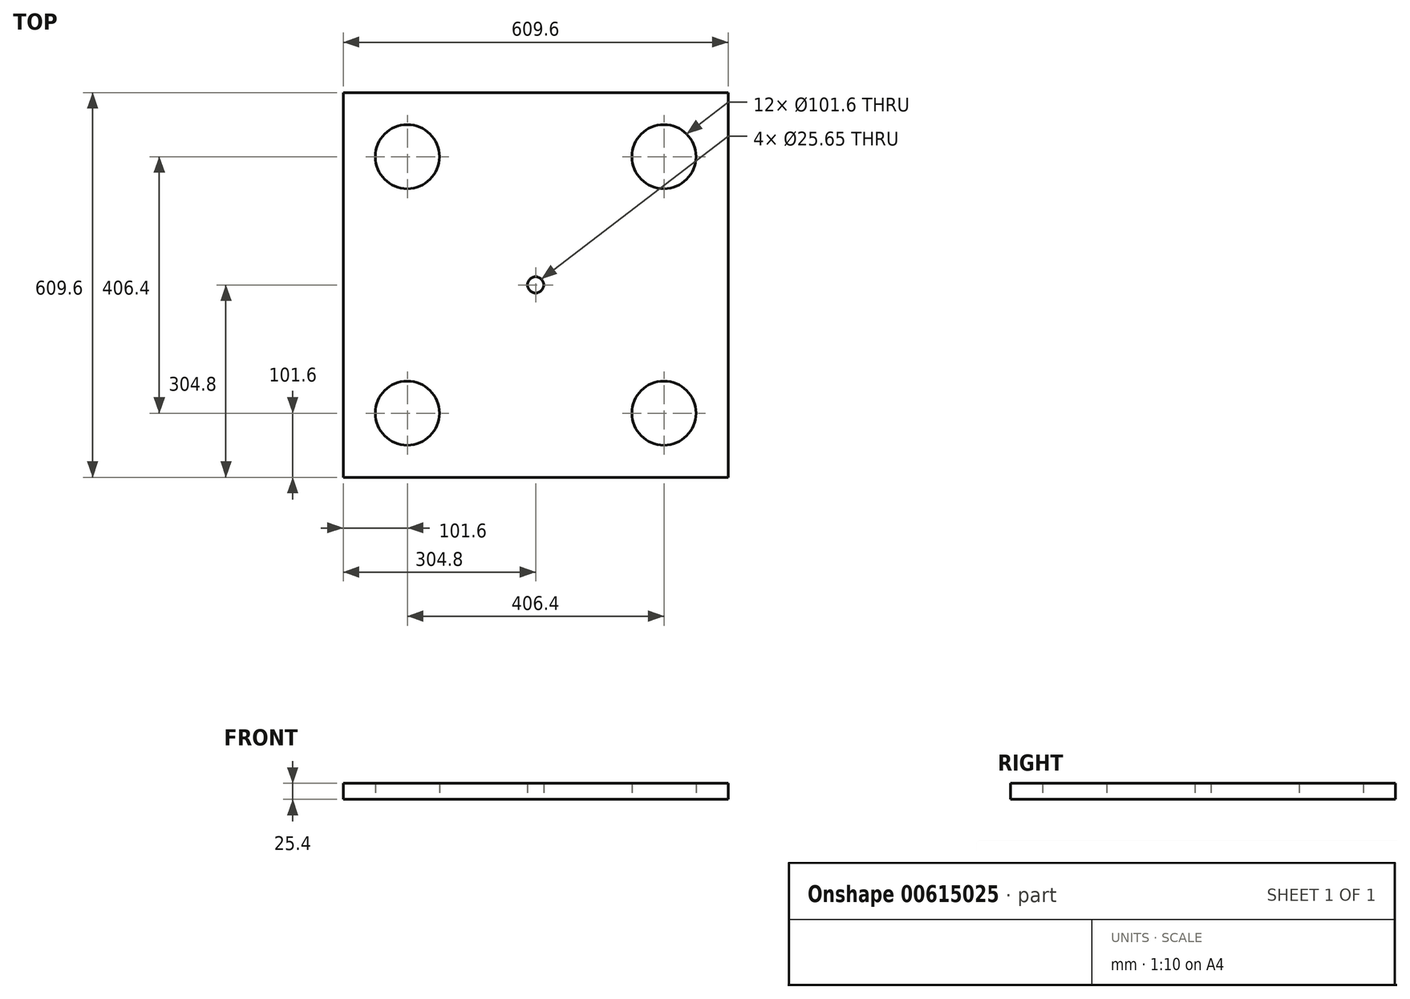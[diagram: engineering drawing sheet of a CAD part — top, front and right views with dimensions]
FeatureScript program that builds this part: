
annotation { "Feature Type Name" : "Feature", "Feature Type Description" : "" }
export const myFeature = defineFeature(function(context is Context, id is Id, definition is map)
    precondition{}
    {
        {
            var Q0;
            Q0=qCreatedBy(makeId("Top.planeOp"),FACE);
            var sketch = newSketch(context, id + "F0", { "sketchPlane" : qUnion([Q0])});
            skLineSegment(sketch, "E0.bottom", {"start": v(304.8, 304.8) * mm, "end": v(-304.8, 304.8) * mm});
            skLineSegment(sketch, "E0.top", {"start": v(304.8, -304.8) * mm, "end": v(-304.8, -304.8) * mm});
            skLineSegment(sketch, "E0.left", {"start": v(304.8, 304.8) * mm, "end": v(304.8, -304.8) * mm});
            skLineSegment(sketch, "E0.right", {"start": v(-304.8, 304.8) * mm, "end": v(-304.8, -304.8) * mm});
            skPoint(sketch, "E0.middle", {"position": v(0, 0) * mm});
            skLineSegment(sketch, "E1.0", {"start": v(203.2, 203.2) * mm, "end": v(-203.2, 203.2) * mm, "construction": true});
            skLineSegment(sketch, "E1.1", {"start": v(203.2, 203.2) * mm, "end": v(203.2, -203.2) * mm, "construction": true});
            skLineSegment(sketch, "E1.2", {"start": v(203.2, -203.2) * mm, "end": v(-203.2, -203.2) * mm, "construction": true});
            skLineSegment(sketch, "E1.3", {"start": v(-203.2, 203.2) * mm, "end": v(-203.2, -203.2) * mm, "construction": true});
            skCircle(sketch, "E2", {"center": v(-203.2, 203.2) * mm, "radius": 50.8 * mm});
            skCircle(sketch, "E3.MirrorC", {"center": v(203.2, 203.2) * mm, "radius": 50.8 * mm});
            skCircle(sketch, "E4.MirrorC", {"center": v(203.2, -203.2) * mm, "radius": 50.8 * mm});
            skCircle(sketch, "E5.MirrorC", {"center": v(-203.2, -203.2) * mm, "radius": 50.8 * mm});
            skCircle(sketch, "E6", {"center": v(0, 0) * mm, "radius": 12.83 * mm});
            skSolve(sketch);
        }
        {
            var Q0;
            Q0=makeQuery(id+"F0.imprint","IMPRINT",FACE,{"disambiguationData":[TD([[makeQuery(id+"F0.imprint","IMPRINT",EDGE,{"derivedFrom":sQuery(id+"F0.wireOp",EDGE,"E0.bottom")}),1.0]])]});
            extrude(context, id + "F1", {"entities" : qUnion([Q0]), "depth" : 25.4 * mm, "offsetDistance" : 25.4 * mm});
        }
        {
            var Q0;
            Q0=makeQuery(id+"F0.imprint","IMPRINT",FACE,{"disambiguationData":[TD([[makeQuery(id+"F0.imprint","IMPRINT",EDGE,{"derivedFrom":sQuery(id+"F0.wireOp",EDGE,"E5.MirrorC")}),-1.0]])]});
            var Q1;
            Q1=makeQuery(id+"F0.imprint","IMPRINT",FACE,{"disambiguationData":[TD([[makeQuery(id+"F0.imprint","IMPRINT",EDGE,{"derivedFrom":sQuery(id+"F0.wireOp",EDGE,"E4.MirrorC")}),1.0]])]});
            var Q2;
            Q2=makeQuery(id+"F0.imprint","IMPRINT",FACE,{"disambiguationData":[TD([[makeQuery(id+"F0.imprint","IMPRINT",EDGE,{"derivedFrom":sQuery(id+"F0.wireOp",EDGE,"E3.MirrorC")}),-1.0]])]});
            var Q3;
            Q3=makeQuery(id+"F0.imprint","IMPRINT",FACE,{"disambiguationData":[TD([[makeQuery(id+"F0.imprint","IMPRINT",EDGE,{"derivedFrom":sQuery(id+"F0.wireOp",EDGE,"E2")}),1.0]])]});
            extrude(context, id + "F2", {"entities" : qUnion([Q0, Q1, Q2, Q3]), "depth" : 25.4 * mm, "offsetDistance" : 25.4 * mm});
        }
    });
